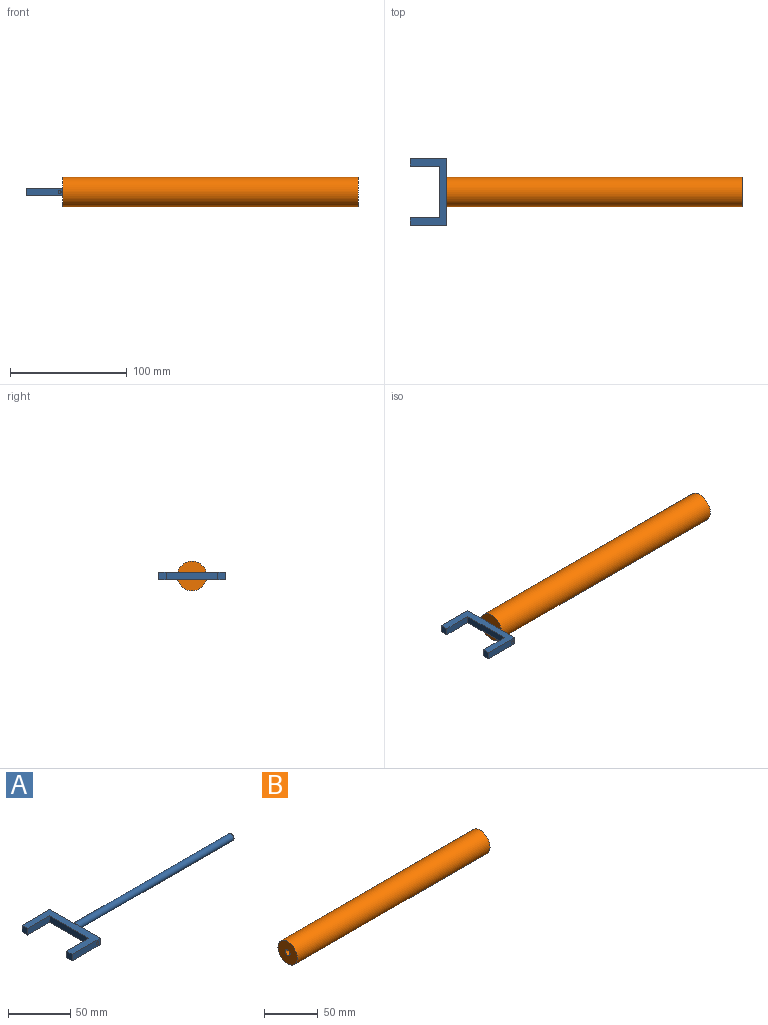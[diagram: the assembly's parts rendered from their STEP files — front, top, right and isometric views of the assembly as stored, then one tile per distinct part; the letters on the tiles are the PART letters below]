
ASSEMBLY  parts=2 mates=1
PART A: 17 faces, bbox 209.6x57.7x6.4 mm
  f0: cylinder r=3.17mm len=177.8mm, axis (1,0,0), area 3546.4mm2, adj f1,f2,f3
  f1: plane 6.35x6.35mm, normal (1,0,0), area 31.7mm2, adj f0
  f2: plane 28.58x6.35mm, normal (1,0,0), area 165.6mm2, adj f0,f4,f5,f8
  f3: plane 28.58x6.35mm, normal (1,0,0), area 165.6mm2, adj f0,f4,f5,f14
  f4: plane 57.15x31.75mm, normal (0,0,1), area 685.5mm2, adj f2,f3,f6,f7,f8,f9,f12,f13
  f5: plane 57.15x31.75mm, normal (0,0,-1), area 685.5mm2, adj f2,f3,f6,f7,f8,f9,f12,f13
  f6: plane 44.45x6.35mm, normal (-1,0,0), area 282.3mm2, adj f4,f5,f9,f12
  f7: plane 6.35x6.35mm, normal (-1,0,0), area 40.3mm2, adj f4,f5,f8,f9
  f8: plane 31.75x6.35mm, normal (0,1,0), area 196.5mm2, adj f2,f4,f5,f7,f10
  f9: plane 25.4x6.35mm, normal (0,-1,0), area 161.3mm2, adj f4,f5,f6,f7
  f10: cylinder r=1.27mm len=2.54mm, axis (0,-1,0), area 2mm2, adj f8,f11
  f11: plane 2.54x2.54mm, normal (0,1,0), area 5.1mm2, adj f10
  f12: plane 25.4x6.35mm, normal (0,1,0), area 161.3mm2, adj f4,f5,f6,f13
  f13: plane 6.35x6.35mm, normal (-1,0,0), area 40.3mm2, adj f4,f5,f12,f14
  f14: plane 31.75x6.35mm, normal (0,-1,0), area 196.5mm2, adj f3,f4,f5,f13,f15
  f15: cylinder r=1.27mm len=2.54mm, axis (0,1,0), area 2mm2, adj f14,f16
  f16: plane 2.54x2.54mm, normal (0,-1,0), area 5.1mm2, adj f15
PART B: 5 faces, bbox 253.2x25.4x25.4 mm
  f0: plane 25.4x25.4mm, normal (-1,0,0), area 475mm2, adj f1,f3
  f1: cylinder r=12.7mm len=253.24mm, axis (-1,0,0), area 20207.5mm2, adj f0,f2
  f2: plane 25.4x25.4mm, normal (1,0,0), area 506.7mm2, adj f1
  f3: cylinder r=3.17mm len=101.6mm, axis (-1,0,0), area 2026.8mm2, adj f0,f4
  f4: plane 6.35x6.35mm, normal (-1,0,0), area 31.7mm2, adj f3
PLACE A t=(177.8,0,0)mm
PLACE B at identity fixed
MATE slider A.f0 <-> B.f1  axis (1,0,0) through (107.95,0,12.7)mm
